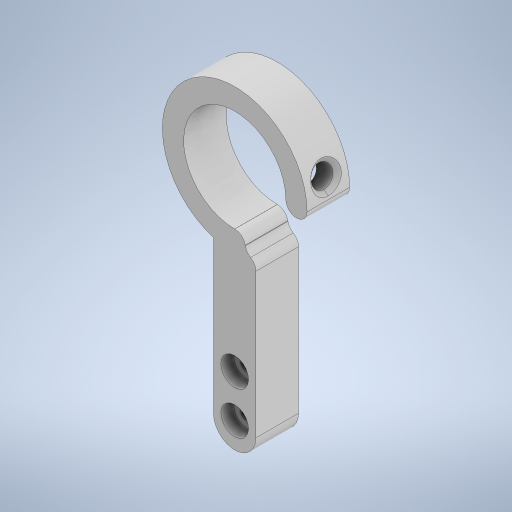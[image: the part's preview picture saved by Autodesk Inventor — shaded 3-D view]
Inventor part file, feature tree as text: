
AUTODESK INVENTOR PART (.ipt)
format: ipt  version: 2023.1 (Build 271208000, 208)  size: 326,144 bytes
history: native  units: mm
features: sketch x4, extrude x3, fillet x2, other x1, revolve x1, chamfer x1
ambient origin geometry x8: Origin, YZ Plane, XZ Plane, XY Plane, X Axis, Y Axis, Z Axis, Center Point
bodies: Body1 (feature_tree)
feature tree (12):
  other  "솔리드1"
  extrude  "돌출1"  Depth=10.0mm
  fillet  "모깎기1"  Radius=45.0mm
  revolve  "회전1"
  chamfer  "모따기1"  Distance=24.0mm
  extrude  "돌출2"  Depth=34.0mm
  fillet  "모깎기2"  Radius=10.0mm
  extrude  "돌출3"  Depth=2.5mm
  sketch  "스케치1"
  sketch  "스케치2"
  sketch  "스케치3"
  sketch  "스케치4"
